# Revit family: Mobile-Work-Tools-Teknion-HDAF_Framed_Fabric_Add_On-R2021
name_source: partatom
category: Furniture
units: mm (PartAtom-declared; Revit-internal decimal feet)

## family parameters
Always vertical = Yes
Cut with Voids When Loaded = No
OmniClass Number = 23.40.20.00
OmniClass Title = General Furniture and Specialties
Room Calculation Point = No
Shared = Yes
Work Plane-Based = No

## types (6) — shared parameters
Assembly Code = E2020200
Manufacturer = Teknion
Manufacturer Fax = 416.661.4586
Part Number = HDAF
Product Documentation Link = https://assets.teknion.com
Product Line = Kiosk
Product Page URL = https://www.teknion.com
Series = Kiosk
Sustainability Data = https://www.teknion.com
URL = www.teknion.com
Unit Weight URL = http://www.teknion.com
Warranty = http://www.teknion.com
zero-valued in all types: Default Elevation

## per-type parameters (varying)
| type | Description | Height | Model | One Bracket | Two Brackets | Width |
| 36" Height x 48" Width | Framed Fabric Add-On, 36" Height, 48" Depth | 36 " | HDAF3648 | No | Yes | 48 " |
| 36" Height x 24" Width | Framed Fabric Add-On, 36" Height, 24" Depth | 36 " | HDAF3624 | Yes | No | 24 " |
| 36" Height x 30" Width | Framed Fabric Add-On, 36" Height, 30" Depth | 36 " | HDAF3630 | Yes | No | 30 " |
| 48" Height x 48" Width | Framed Fabric Add-On, 48" Height, 48" Depth | 48 " | HDAF4848 | No | Yes | 48 " |
| 48" Height x 24" Width | Framed Fabric Add-On, 48" Height, 24" Depth | 48 " | HDAF4824 | Yes | No | 24 " |
| 48" Height x 30" Width | Framed Fabric Add-On, 48" Height, 30" Depth | 48 " | HDAF4830 | Yes | No | 30 " |

## geometry (parser evidence)
native form markers: Sweep x3
no freeform markers — native parametric forms only
